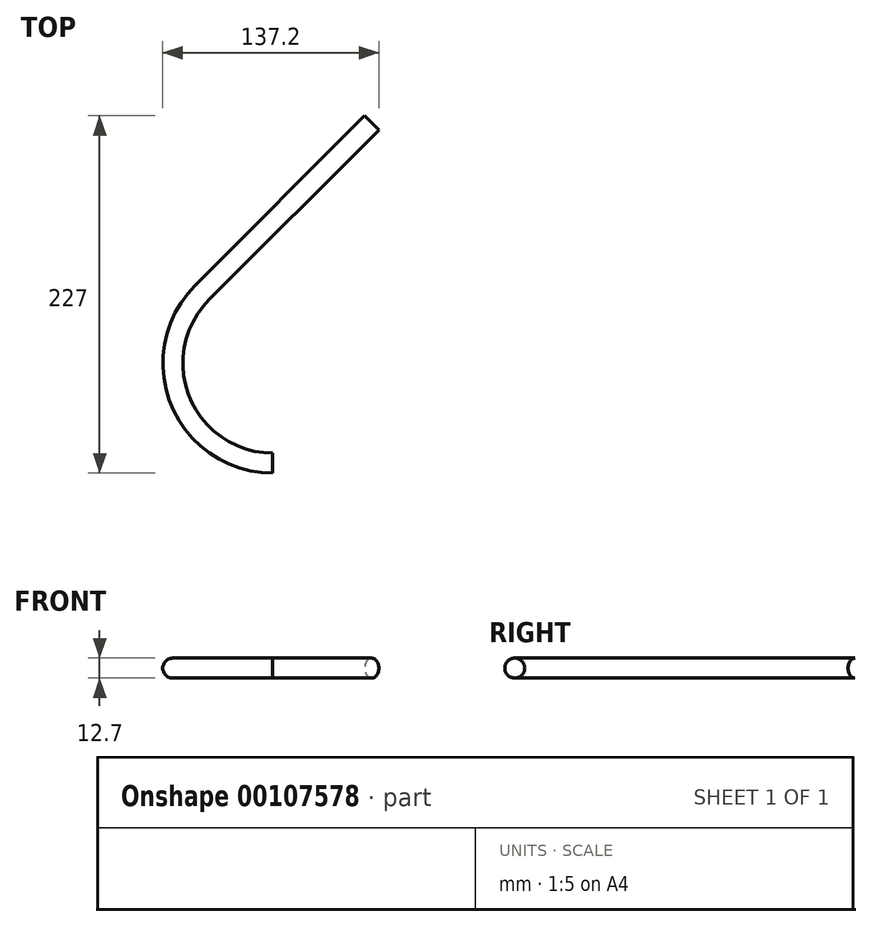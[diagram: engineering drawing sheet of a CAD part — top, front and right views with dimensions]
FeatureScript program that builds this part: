
annotation { "Feature Type Name" : "Feature", "Feature Type Description" : "" }
export const myFeature = defineFeature(function(context is Context, id is Id, definition is map)
    precondition{}
    {
        {
            var Q0;
            Q0=qCreatedBy(makeId("Right.planeOp"),FACE);
            var sketch = newSketch(context, id + "F0", { "sketchPlane" : qUnion([Q0])});
            skCircle(sketch, "E0", {"center": v(-63.5, 0) * mm, "radius": 6.35 * mm});
            skLineSegment(sketch, "E1", {"start": v(0, 47.9) * mm, "end": v(0, -53.12) * mm, "construction": true});
            skSolve(sketch);
        }
        {
            var Q0;
            Q0 = qSketchRegion(id + "F0", true);
            var Q1;
            Q1=sQuery(id+"F0.wireOp",EDGE,"E1");
            revolve(context, id + "F1", {"entities" : qUnion([Q0]), "axis" : qUnion([Q1]), "revolveType" : RevolveType.ONE_DIRECTION, "angle" : 135 * degree});
        }
        {
            var Q0;
            Q0=makeQuery(id+"F1.opRevolve","CAP_FACE",FACE,{"disambiguationData":[OSD([sQuery(id+"F0.wireOp",EDGE,"E0")])],"isStart":false});
            var sketch = newSketch(context, id + "F2", { "sketchPlane" : qUnion([Q0])});
            skCircle(sketch, "E2", {"center": v(63.5, 0) * mm, "radius": 6.35 * mm});
            skSolve(sketch);
        }
        {
            var Q0;
            Q0 = qSketchRegion(id + "F2", true);
            extrude(context, id + "F3", {"entities" : qUnion([Q0]), "operationType" : NewBodyOperationType.ADD, "depth" : 152.4 * mm});
        }
    });
